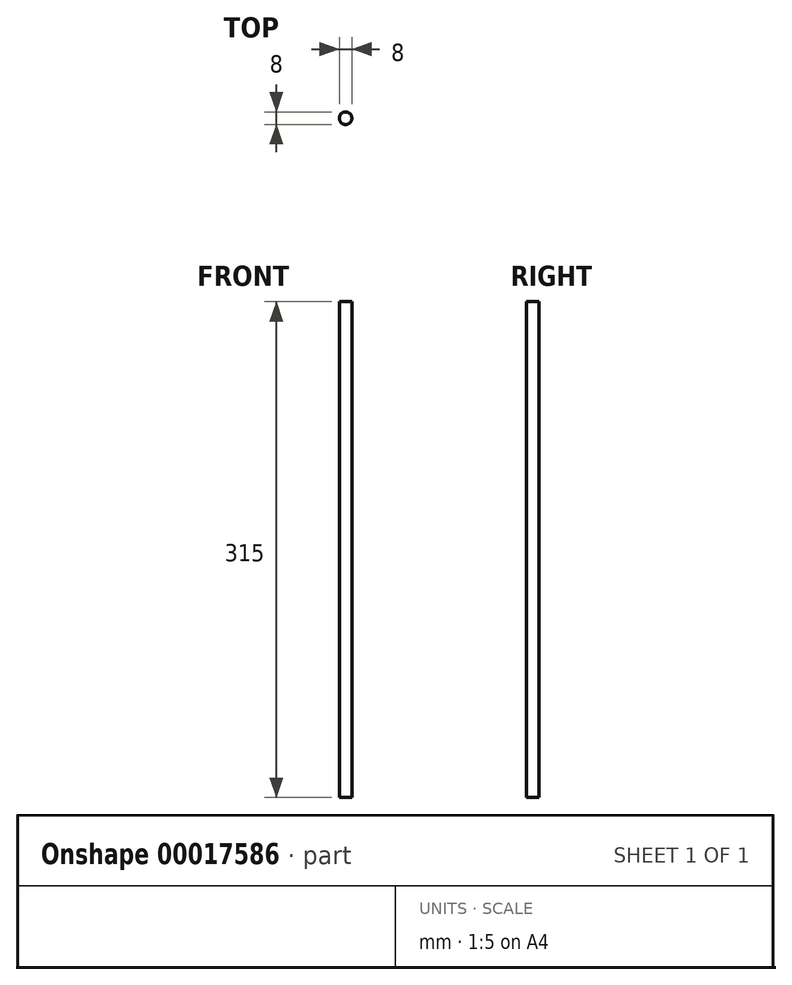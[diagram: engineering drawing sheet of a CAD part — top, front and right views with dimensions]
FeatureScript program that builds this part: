
annotation { "Feature Type Name" : "Feature", "Feature Type Description" : "" }
export const myFeature = defineFeature(function(context is Context, id is Id, definition is map)
    precondition{}
    {
        {
            var Q0;
            Q0=qCreatedBy(makeId("Top.planeOp"),FACE);
            var sketch = newSketch(context, id + "F0", { "sketchPlane" : qUnion([Q0])});
            skCircle(sketch, "E0", {"center": v(0, 0) * mm, "radius": 4 * mm});
            skSolve(sketch);
        }
        {
            var Q0;
            Q0=qSketchRegion(id+"F0",true);
            extrude(context, id + "F1", {"entities" : qUnion([Q0]), "depth" : 315 * mm});
        }
    });
